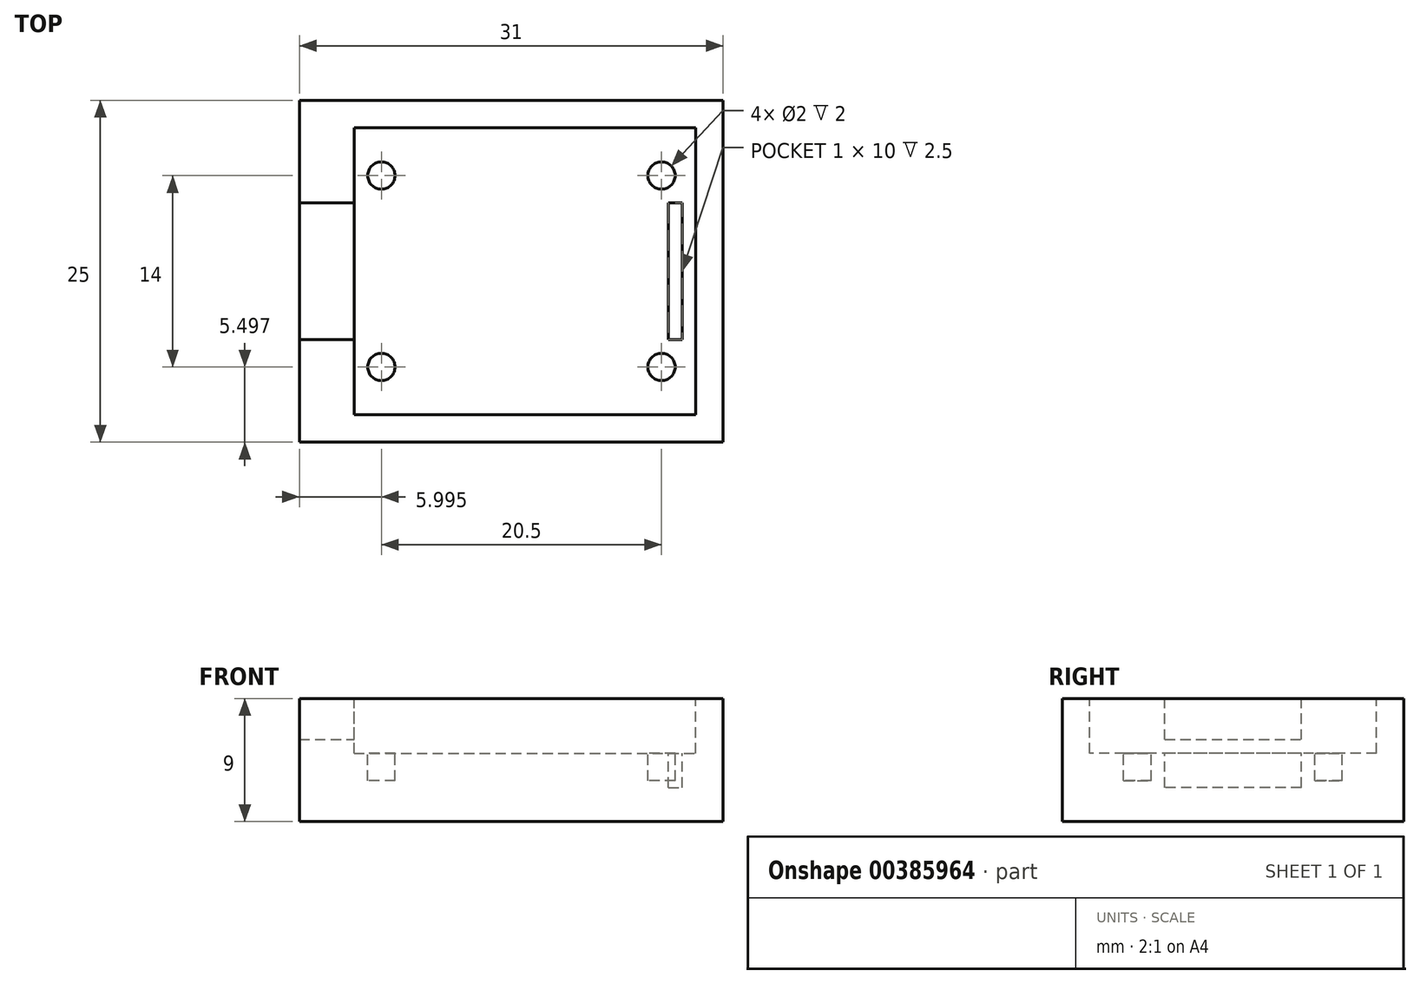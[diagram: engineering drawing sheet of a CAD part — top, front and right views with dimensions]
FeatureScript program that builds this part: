
annotation { "Feature Type Name" : "Feature", "Feature Type Description" : "" }
export const myFeature = defineFeature(function(context is Context, id is Id, definition is map)
    precondition{}
    {
        {
            var Q0;
            Q0=qCreatedBy(makeId("Top.planeOp"),FACE);
            var sketch = newSketch(context, id + "F0", { "sketchPlane" : qUnion([Q0])});
            skLineSegment(sketch, "E0.bottom", {"start": v(-10.35, 10.53) * mm, "end": v(20.65, 10.53) * mm});
            skLineSegment(sketch, "E0.top", {"start": v(-10.35, -14.47) * mm, "end": v(20.65, -14.47) * mm});
            skLineSegment(sketch, "E0.left", {"start": v(-10.35, 10.53) * mm, "end": v(-10.35, -14.47) * mm});
            skLineSegment(sketch, "E0.right", {"start": v(20.65, 10.53) * mm, "end": v(20.65, -14.47) * mm});
            skSolve(sketch);
        }
        {
            var Q0;
            Q0=qSketchRegion(id+"F0",true);
            extrude(context, id + "F1", {"entities" : qUnion([Q0]), "depth" : 9 * mm});
        }
        {
            var Q0;
            Q0=makeQuery(id+"F1.opExtrude","CAP_FACE",FACE,{"disambiguationData":[OSD([sQuery(id+"F0.wireOp",EDGE,"E0.bottom"),sQuery(id+"F0.wireOp",EDGE,"E0.top"),sQuery(id+"F0.wireOp",EDGE,"E0.left"),sQuery(id+"F0.wireOp",EDGE,"E0.right")])],"isStart":false});
            var sketch = newSketch(context, id + "F2", { "sketchPlane" : qUnion([Q0])});
            skLineSegment(sketch, "E1.bottom", {"start": v(-6.35, 8.53) * mm, "end": v(18.65, 8.53) * mm});
            skLineSegment(sketch, "E1.top", {"start": v(-6.35, -12.47) * mm, "end": v(18.65, -12.47) * mm});
            skLineSegment(sketch, "E1.left", {"start": v(-6.35, 8.53) * mm, "end": v(-6.35, -12.47) * mm});
            skLineSegment(sketch, "E1.right", {"start": v(18.65, 8.53) * mm, "end": v(18.65, -12.47) * mm});
            skSolve(sketch);
        }
        {
            var Q0;
            Q0=qSketchRegion(id+"F2",true);
            extrude(context, id + "F3", {"entities" : qUnion([Q0]), "operationType" : NewBodyOperationType.REMOVE, "oppositeDirection" : true, "depth" : 4 * mm});
        }
        {
            var Q0;
            Q0=makeQuery(id+"F1.opExtrude","CAP_FACE",FACE,{"disambiguationData":[OSD([sQuery(id+"F0.wireOp",EDGE,"E0.bottom"),sQuery(id+"F0.wireOp",EDGE,"E0.top"),sQuery(id+"F0.wireOp",EDGE,"E0.left"),sQuery(id+"F0.wireOp",EDGE,"E0.right")])],"isStart":false});
            var sketch = newSketch(context, id + "F4", { "sketchPlane" : qUnion([Q0])});
            skLineSegment(sketch, "E2.bottom", {"start": v(-10.35, 3.03) * mm, "end": v(16.65, 3.03) * mm});
            skLineSegment(sketch, "E2.top", {"start": v(-10.35, -6.97) * mm, "end": v(16.65, -6.97) * mm});
            skLineSegment(sketch, "E2.left", {"start": v(-10.35, 3.03) * mm, "end": v(-10.35, -6.97) * mm});
            skLineSegment(sketch, "E2.right", {"start": v(16.65, 3.03) * mm, "end": v(16.65, -6.97) * mm});
            skLineSegment(sketch, "E3.bottom", {"start": v(-0.35, 3.03) * mm, "end": v(1.65, 3.03) * mm});
            skLineSegment(sketch, "E3.top", {"start": v(-0.35, 4.03) * mm, "end": v(1.65, 4.03) * mm});
            skLineSegment(sketch, "E3.left", {"start": v(-0.35, 3.03) * mm, "end": v(-0.35, 4.03) * mm});
            skLineSegment(sketch, "E3.right", {"start": v(1.65, 3.03) * mm, "end": v(1.65, 4.03) * mm});
            skLineSegment(sketch, "E4.bottom", {"start": v(11.65, 3.03) * mm, "end": v(13.65, 3.03) * mm});
            skLineSegment(sketch, "E4.top", {"start": v(11.65, 4.03) * mm, "end": v(13.65, 4.03) * mm});
            skLineSegment(sketch, "E4.left", {"start": v(11.65, 3.03) * mm, "end": v(11.65, 4.03) * mm});
            skLineSegment(sketch, "E4.right", {"start": v(13.65, 3.03) * mm, "end": v(13.65, 4.03) * mm});
            skLineSegment(sketch, "E5.bottom", {"start": v(-0.35, -6.97) * mm, "end": v(1.65, -6.97) * mm});
            skLineSegment(sketch, "E5.top", {"start": v(-0.35, -7.97) * mm, "end": v(1.65, -7.97) * mm});
            skLineSegment(sketch, "E5.left", {"start": v(-0.35, -6.97) * mm, "end": v(-0.35, -7.97) * mm});
            skLineSegment(sketch, "E5.right", {"start": v(1.65, -6.97) * mm, "end": v(1.65, -7.97) * mm});
            skLineSegment(sketch, "E6.bottom", {"start": v(11.65, -6.97) * mm, "end": v(13.65, -6.97) * mm});
            skLineSegment(sketch, "E6.top", {"start": v(11.65, -7.97) * mm, "end": v(13.65, -7.97) * mm});
            skLineSegment(sketch, "E6.left", {"start": v(11.65, -6.97) * mm, "end": v(11.65, -7.97) * mm});
            skLineSegment(sketch, "E6.right", {"start": v(13.65, -6.97) * mm, "end": v(13.65, -7.97) * mm});
            skLineSegment(sketch, "E7.bottom", {"start": v(16.65, 3.03) * mm, "end": v(17.65, 3.03) * mm});
            skLineSegment(sketch, "E7.top", {"start": v(16.65, -6.97) * mm, "end": v(17.65, -6.97) * mm});
            skLineSegment(sketch, "E7.right", {"start": v(17.65, 3.03) * mm, "end": v(17.65, -6.97) * mm});
            skSolve(sketch);
        }
        {
            var Q0;
            Q0=makeQuery(id+"F4.imprint","IMPRINT",FACE,{"disambiguationData":[TD([[makeQuery(id+"F4.imprint","IMPRINT",EDGE,{"derivedFrom":sQuery(id+"F4.wireOp",EDGE,"E3.bottom")}),1.0]])]});
            var Q1;
            Q1=makeQuery(id+"F4.imprint","IMPRINT",FACE,{"disambiguationData":[TD([[makeQuery(id+"F4.imprint","IMPRINT",EDGE,{"derivedFrom":sQuery(id+"F4.wireOp",EDGE,"E4.bottom")}),1.0]])]});
            var Q2;
            Q2=makeQuery(id+"F4.imprint","IMPRINT",FACE,{"disambiguationData":[TD([[makeQuery(id+"F4.imprint","IMPRINT",EDGE,{"derivedFrom":sQuery(id+"F4.wireOp",EDGE,"E5.bottom")}),-1.0]])]});
            var Q3;
            Q3=makeQuery(id+"F4.imprint","IMPRINT",FACE,{"disambiguationData":[TD([[makeQuery(id+"F4.imprint","IMPRINT",EDGE,{"derivedFrom":sQuery(id+"F4.wireOp",EDGE,"E6.bottom")}),-1.0]])]});
            var Q4;
            Q4=makeQuery(id+"F4.imprint","IMPRINT",FACE,{"disambiguationData":[TD([[makeQuery(id+"F4.imprint","IMPRINT",EDGE,{"derivedFrom":sQuery(id+"F4.wireOp",EDGE,"E7.bottom")}),-1.0]])]});
            var Q5;
            {var subQ1=sQuery(id+"F4.wireOp",EDGE,"E3.bottom");Q5=makeQuery(id+"F4.imprint","IMPRINT",FACE,{"disambiguationData":[TD([[makeQuery(id+"F4.imprint","IMPRINT",EDGE,{"derivedFrom":subQ1}),-1.0]])]});}
            extrude(context, id + "F5", {"entities" : qUnion([Q0, Q1, Q2, Q3, Q4, Q5]), "operationType" : NewBodyOperationType.REMOVE, "oppositeDirection" : true, "depth" : 6.5 * mm});
        }
        {
            var Q0;
            Q0=makeQuery(id+"F3.boolean.opBoolean","COPY",FACE,{"derivedFrom":makeQuery(id+"F3.opExtrude","CAP_FACE",FACE,{"disambiguationData":[OSD([sQuery(id+"F2.wireOp",EDGE,"E1.bottom"),sQuery(id+"F2.wireOp",EDGE,"E1.top"),sQuery(id+"F2.wireOp",EDGE,"E1.left"),sQuery(id+"F2.wireOp",EDGE,"E1.right")])],"isStart":false})});
            var sketch = newSketch(context, id + "F6", { "sketchPlane" : qUnion([Q0])});
            skCircle(sketch, "E8", {"center": v(-4.35, 5.03) * mm, "radius": 1 * mm});
            skCircle(sketch, "E9", {"center": v(16.15, 5.03) * mm, "radius": 1 * mm});
            skCircle(sketch, "E10", {"center": v(-4.35, -8.97) * mm, "radius": 1 * mm});
            skCircle(sketch, "E11", {"center": v(16.15, -8.97) * mm, "radius": 1 * mm});
            skSolve(sketch);
        }
        {
            var Q0;
            Q0=qSketchRegion(id+"F6",true);
            extrude(context, id + "F7", {"entities" : qUnion([Q0]), "operationType" : NewBodyOperationType.REMOVE, "oppositeDirection" : true, "depth" : 2 * mm});
        }
        {
            var Q0;
            Q0=qSketchRegion(id+"F4",true);
            extrude(context, id + "F8", {"entities" : qUnion([Q0]), "operationType" : NewBodyOperationType.REMOVE, "oppositeDirection" : true, "depth" : 1 * mm});
        }
        {
            var Q0;
            Q0=makeQuery(id+"F8.boolean.opBoolean","COPY",FACE,{"derivedFrom":makeQuery(id+"F8.opExtrude","CAP_FACE",FACE,{"disambiguationData":[OSD([sQuery(id+"F4.wireOp",EDGE,"E2.bottom"),sQuery(id+"F4.wireOp",EDGE,"E2.top"),sQuery(id+"F4.wireOp",EDGE,"E2.left"),sQuery(id+"F4.wireOp",EDGE,"E3.top"),sQuery(id+"F4.wireOp",EDGE,"E3.left"),sQuery(id+"F4.wireOp",EDGE,"E3.right"),sQuery(id+"F4.wireOp",EDGE,"E4.top"),sQuery(id+"F4.wireOp",EDGE,"E4.left"),sQuery(id+"F4.wireOp",EDGE,"E4.right"),sQuery(id+"F4.wireOp",EDGE,"E5.top"),sQuery(id+"F4.wireOp",EDGE,"E5.left"),sQuery(id+"F4.wireOp",EDGE,"E5.right"),sQuery(id+"F4.wireOp",EDGE,"E6.top"),sQuery(id+"F4.wireOp",EDGE,"E6.left"),sQuery(id+"F4.wireOp",EDGE,"E6.right"),sQuery(id+"F4.wireOp",EDGE,"E7.bottom"),sQuery(id+"F4.wireOp",EDGE,"E7.top"),sQuery(id+"F4.wireOp",EDGE,"E7.right")])],"isStart":false})});
            extrude(context, id + "F9", {"entities" : qUnion([Q0]), "operationType" : NewBodyOperationType.REMOVE, "oppositeDirection" : true, "depth" : 2 * mm});
        }
    });
